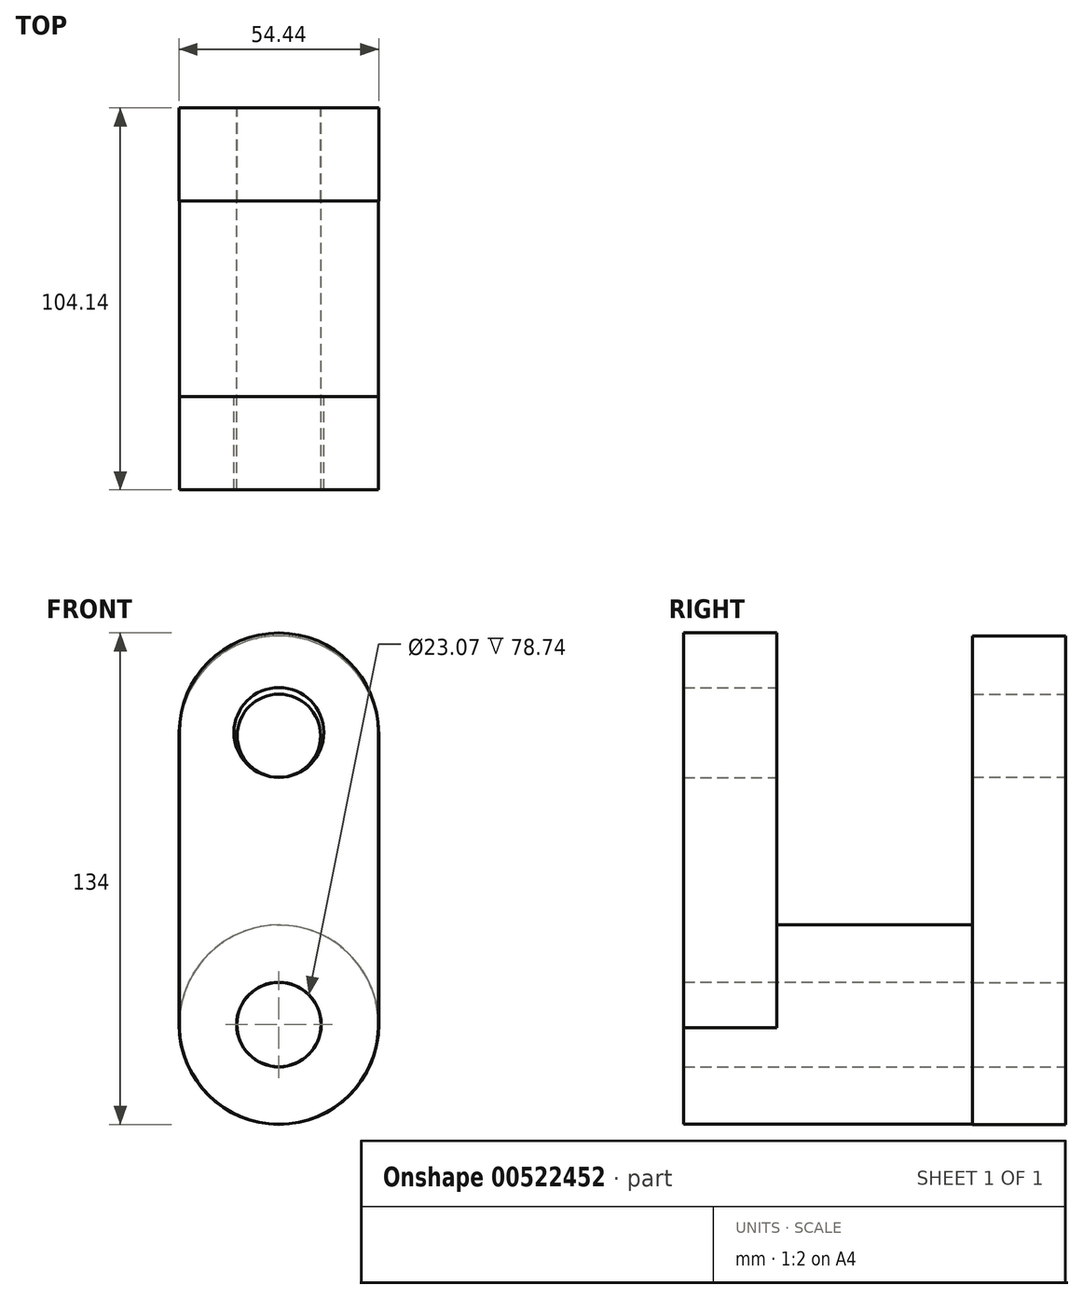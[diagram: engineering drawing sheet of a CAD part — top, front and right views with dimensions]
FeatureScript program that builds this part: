
annotation { "Feature Type Name" : "Feature", "Feature Type Description" : "" }
export const myFeature = defineFeature(function(context is Context, id is Id, definition is map)
    precondition{}
    {
        {
            var Q0;
            Q0=qCreatedBy(makeId("Front.planeOp"),FACE);
            var sketch = newSketch(context, id + "F0", { "sketchPlane" : qUnion([Q0])});
            skLineSegment(sketch, "E0.left", {"start": v(27.22, -39.38) * mm, "end": v(27.22, 39.38) * mm});
            skLineSegment(sketch, "E0.right", {"start": v(-27.22, -39.38) * mm, "end": v(-27.22, 39.38) * mm});
            skPoint(sketch, "E0.middle", {"position": v(0, 0) * mm});
            skCircle(sketch, "E1", {"center": v(0, 39.38) * mm, "radius": 27.22 * mm});
            skCircle(sketch, "E2", {"center": v(0, -39.38) * mm, "radius": 27.22 * mm});
            skCircle(sketch, "E3", {"center": v(0, 39.38) * mm, "radius": 11.35 * mm});
            skCircle(sketch, "E4", {"center": v(0, -39.38) * mm, "radius": 11.47 * mm});
            skSolve(sketch);
        }
        {
            var Q0;
            Q0 = qSketchRegion(id + "F0", true);
            extrude(context, id + "F1", {"entities" : qUnion([Q0]), "depth" : 25.4 * mm, "offsetDistance" : 25.4 * mm});
        }
        {
            var Q0;
            Q0=makeQuery(id+"F1.opExtrude","CAP_FACE",FACE,{"disambiguationData":[OSD([sQuery(id+"F0.wireOp",EDGE,"E0.left"),sQuery(id+"F0.wireOp",EDGE,"E0.right"),sQuery(id+"F0.wireOp",EDGE,"E1"),sQuery(id+"F0.wireOp",EDGE,"E2"),sQuery(id+"F0.wireOp",EDGE,"E3"),sQuery(id+"F0.wireOp",EDGE,"E4")])],"isStart":false});
            var sketch = newSketch(context, id + "F2", { "sketchPlane" : qUnion([Q0])});
            skCircle(sketch, "E5", {"center": v(0, -39.38) * mm, "radius": 27.15 * mm});
            skCircle(sketch, "E6", {"center": v(0, -39.38) * mm, "radius": 11.53 * mm});
            skSolve(sketch);
        }
        {
            var Q0;
            Q0 = qSketchRegion(id + "F2", true);
            extrude(context, id + "F3", {"entities" : qUnion([Q0]), "operationType" : NewBodyOperationType.ADD, "depth" : 53.34 * mm, "offsetDistance" : 25.4 * mm});
        }
        {
            var Q0;
            Q0=makeQuery(id+"F3.opExtrude","CAP_FACE",FACE,{"disambiguationData":[OSD([sQuery(id+"F2.wireOp",EDGE,"E5"),sQuery(id+"F2.wireOp",EDGE,"E6")])],"isStart":false});
            var sketch = newSketch(context, id + "F4", { "sketchPlane" : qUnion([Q0])});
            skLineSegment(sketch, "E7.left", {"start": v(27.14, -40.26) * mm, "end": v(27.14, 40.26) * mm});
            skLineSegment(sketch, "E7.right", {"start": v(-27.14, -40.26) * mm, "end": v(-27.14, 40.26) * mm});
            skPoint(sketch, "E7.middle", {"position": v(0, 0) * mm});
            skCircle(sketch, "E8", {"center": v(0, 40.26) * mm, "radius": 27.14 * mm});
            skCircle(sketch, "E9", {"center": v(0, 40.26) * mm, "radius": 12.24 * mm});
            skCircle(sketch, "E10", {"center": v(0, -40.26) * mm, "radius": 12.35 * mm});
            skSolve(sketch);
        }
        {
            var Q0;
            Q0=makeQuery(id+"F4.imprint","IMPRINT",FACE,{"disambiguationData":[TD([[makeQuery(id+"F4.imprint","IMPRINT",EDGE,{"derivedFrom":sQuery(id+"F4.wireOp",EDGE,"E9")}),-1.0]])]});
            var Q1;
            {var subQ0=sQuery(id+"F4.wireOp",EDGE,"E10");var subQ1=makeQuery(id+"F3.opExtrude","CAP_EDGE",EDGE,{"disambiguationData":[OSD([sQuery(id+"F2.wireOp",EDGE,"E6")])],"isStart":false});var subQ2=makeQuery(id+"F4.imprint","INTERSECT",VERTEX,{"disambiguationData":[OD(0.0)],"derivedFrom":[subQ1,subQ0]});Q1=makeQuery(id+"F4.imprint","IMPRINT",FACE,{"disambiguationData":[TD([[makeQuery(id+"F4.imprint","IMPRINT",EDGE,{"disambiguationData":[TD([[subQ2,-1.0]])],"derivedFrom":subQ0}),1.0]])]});}
            var Q2;
            {var subQ0=sQuery(id+"F4.wireOp",EDGE,"E8");var subQ1=sQuery(id+"F4.wireOp",EDGE,"E7.left");var subQ2=makeQuery(id+"F4.imprint","INTERSECT",VERTEX,{"derivedFrom":[subQ1,subQ0]});Q2=makeQuery(id+"F4.imprint","IMPRINT",FACE,{"disambiguationData":[TD([[makeQuery(id+"F4.imprint","IMPRINT",EDGE,{"disambiguationData":[TD([[subQ2,1.0]])],"derivedFrom":subQ1}),1.0]])]});}
            var Q3;
            {var subQ0=sQuery(id+"F4.wireOp",EDGE,"E7.left");var subQ1=makeQuery(id+"F3.opExtrude","CAP_EDGE",EDGE,{"disambiguationData":[OSD([sQuery(id+"F2.wireOp",EDGE,"E5")])],"isStart":false});var subQ2=makeQuery(id+"F4.imprint","INTERSECT",VERTEX,{"disambiguationData":[OD(0.0)],"derivedFrom":[subQ1,subQ0]});Q3=makeQuery(id+"F4.imprint","IMPRINT",FACE,{"disambiguationData":[TD([[makeQuery(id+"F4.imprint","IMPRINT",EDGE,{"disambiguationData":[TD([[subQ2,-1.0]])],"derivedFrom":subQ0}),1.0]])]});}
            extrude(context, id + "F5", {"entities" : qUnion([Q0, Q1, Q2, Q3]), "operationType" : NewBodyOperationType.ADD, "depth" : 25.4 * mm, "offsetDistance" : 25.4 * mm});
        }
    });
